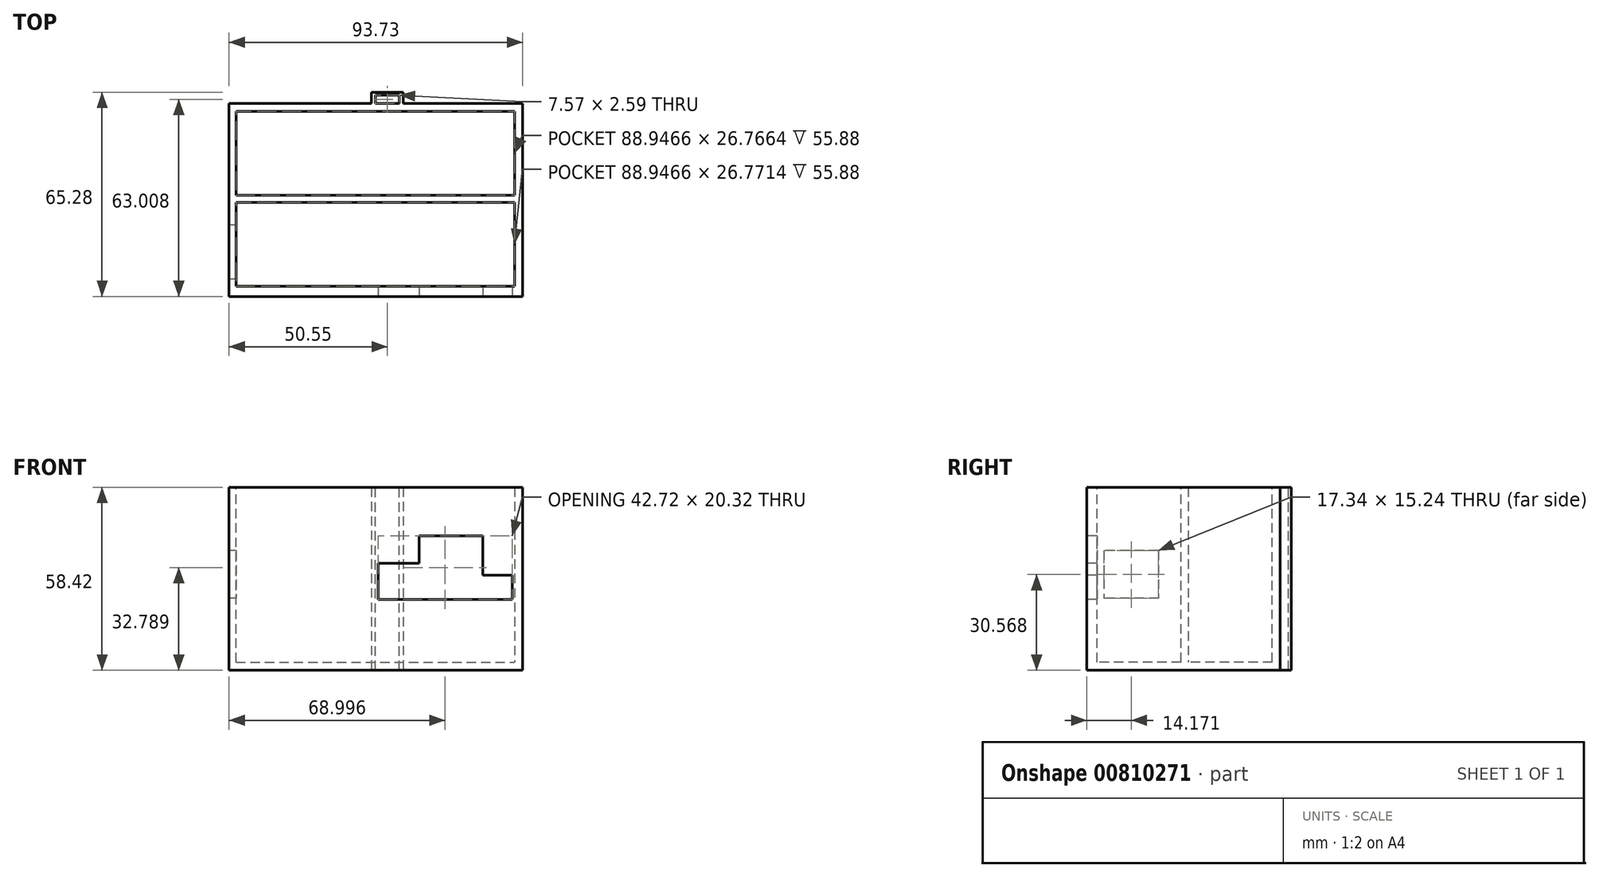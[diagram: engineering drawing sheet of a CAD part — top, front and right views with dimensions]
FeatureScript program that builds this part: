
annotation { "Feature Type Name" : "Feature", "Feature Type Description" : "" }
export const myFeature = defineFeature(function(context is Context, id is Id, definition is map)
    precondition{}
    {
        {
            var Q0;
            Q0=qCreatedBy(makeId("Front.planeOp"),FACE);
            var sketch = newSketch(context, id + "F0", { "sketchPlane" : qUnion([Q0])});
            skLineSegment(sketch, "E0.bottom", {"start": v(-45.72, 29.21) * mm, "end": v(40.64, 29.21) * mm});
            skLineSegment(sketch, "E0.top", {"start": v(-45.72, -29.21) * mm, "end": v(40.64, -29.21) * mm});
            skLineSegment(sketch, "E0.left", {"start": v(-45.72, 29.21) * mm, "end": v(-45.72, -29.21) * mm});
            skLineSegment(sketch, "E0.right", {"start": v(40.64, 29.21) * mm, "end": v(40.64, -29.21) * mm});
            skPoint(sketch, "E0.middle", {"position": v(-2.54, 0) * mm});
            skSolve(sketch);
        }
        {
            var Q0;
            Q0=makeQuery(id+"F0.imprint","IMPRINT",FACE,{"disambiguationData":[TD([[makeQuery(id+"F0.imprint","IMPRINT",EDGE,{"derivedFrom":sQuery(id+"F0.wireOp",EDGE,"E0.bottom")}),-1.0]])]});
            extrude(context, id + "F1", {"entities" : qUnion([Q0]), "oppositeDirection" : true, "depth" : 61.72 * mm, "offsetDistance" : 25.4 * mm});
        }
        {
            var Q0;
            Q0=makeQuery(id+"F1.opExtrude","CAP_FACE",FACE,{"disambiguationData":[OSD([sQuery(id+"F0.wireOp",EDGE,"E0.bottom"),sQuery(id+"F0.wireOp",EDGE,"E0.top"),sQuery(id+"F0.wireOp",EDGE,"E0.left"),sQuery(id+"F0.wireOp",EDGE,"E0.right")])],"isStart":true});
            var sketch = newSketch(context, id + "F2", { "sketchPlane" : qUnion([Q0])});
            skLineSegment(sketch, "E1", {"start": v(-45.72, 29.21) * mm, "end": v(-45.72, 13.74) * mm});
            skLineSegment(sketch, "E2", {"start": v(7.56, 13.74) * mm, "end": v(27.88, 13.74) * mm});
            skLineSegment(sketch, "E3", {"start": v(27.88, 13.74) * mm, "end": v(27.88, -6.58) * mm});
            skLineSegment(sketch, "E4", {"start": v(27.88, -6.58) * mm, "end": v(7.56, -6.58) * mm});
            skLineSegment(sketch, "E5", {"start": v(7.56, -6.58) * mm, "end": v(7.56, 13.74) * mm});
            skLineSegment(sketch, "E6", {"start": v(27.88, 1.12) * mm, "end": v(27.88, -6.58) * mm});
            skLineSegment(sketch, "E7", {"start": v(37.27, 1.12) * mm, "end": v(37.27, -6.58) * mm});
            skLineSegment(sketch, "E8", {"start": v(27.88, 1.12) * mm, "end": v(37.27, 1.12) * mm});
            skLineSegment(sketch, "E9", {"start": v(37.27, -6.58) * mm, "end": v(27.88, -6.58) * mm});
            skLineSegment(sketch, "E10.bottom", {"start": v(7.56, -6.58) * mm, "end": v(-5.45, -6.58) * mm});
            skLineSegment(sketch, "E10.top", {"start": v(7.56, 4.93) * mm, "end": v(-5.45, 4.93) * mm});
            skLineSegment(sketch, "E10.left", {"start": v(7.56, -6.58) * mm, "end": v(7.56, 4.93) * mm});
            skLineSegment(sketch, "E10.right", {"start": v(-5.45, -6.58) * mm, "end": v(-5.45, 4.93) * mm});
            skSolve(sketch);
        }
        {
            var Q0;
            Q0 = qSketchRegion(id + "F2", true);
            extrude(context, id + "F3", {"entities" : qUnion([Q0]), "operationType" : NewBodyOperationType.REMOVE, "oppositeDirection" : true, "depth" : 56.64 * mm, "offsetDistance" : 25.4 * mm});
        }
        {
            var Q0;
            Q0=makeQuery(id+"F1.opExtrude","SWEPT_FACE",FACE,{"disambiguationData":[OSD([sQuery(id+"F0.wireOp",EDGE,"E0.bottom")])]});
            var sketch = newSketch(context, id + "F4", { "sketchPlane" : qUnion([Q0])});
            skLineSegment(sketch, "E11", {"start": v(-43.12, 0) * mm, "end": v(37.96, 0) * mm});
            skLineSegment(sketch, "E12", {"start": v(37.96, 61.72) * mm, "end": v(-43.18, 61.72) * mm});
            skLineSegment(sketch, "E13", {"start": v(-43.18, 59.18) * mm, "end": v(38.1, 59.18) * mm});
            skLineSegment(sketch, "E14", {"start": v(38.1, 3.3) * mm, "end": v(-43.18, 3.3) * mm});
            skLineSegment(sketch, "E15", {"start": v(-43.18, 59.18) * mm, "end": v(-43.18, 3.3) * mm});
            skLineSegment(sketch, "E16", {"start": v(38.1, 59.18) * mm, "end": v(38.1, 3.3) * mm});
            skSolve(sketch);
        }
        {
            var Q0;
            Q0 = qSketchRegion(id + "F4", true);
            extrude(context, id + "F5", {"entities" : qUnion([Q0]), "operationType" : NewBodyOperationType.REMOVE, "oppositeDirection" : true, "depth" : 55.88 * mm, "offsetDistance" : 25.4 * mm});
        }
        {
            var Q0;
            Q0=makeQuery(id+"F5.boolean.opBoolean","COPY",FACE,{"derivedFrom":makeQuery(id+"F5.opExtrude","CAP_FACE",FACE,{"disambiguationData":[OSD([sQuery(id+"F4.wireOp",EDGE,"E13"),sQuery(id+"F4.wireOp",EDGE,"E14"),sQuery(id+"F4.wireOp",EDGE,"E15"),sQuery(id+"F4.wireOp",EDGE,"E16")])],"isStart":false})});
            var sketch = newSketch(context, id + "F6", { "sketchPlane" : qUnion([Q0])});
            skLineSegment(sketch, "E17", {"start": v(-43.18, 16.72) * mm, "end": v(-43.18, 32.42) * mm});
            skLineSegment(sketch, "E18", {"start": v(-43.18, 32.42) * mm, "end": v(38.1, 32.42) * mm});
            skLineSegment(sketch, "E19", {"start": v(38.1, 32.42) * mm, "end": v(38.1, 16.72) * mm});
            skLineSegment(sketch, "E20", {"start": v(-43.18, 30.07) * mm, "end": v(38.1, 30.07) * mm});
            skSolve(sketch);
        }
        {
            var Q0;
            Q0 = qSketchRegion(id + "F6", true);
            extrude(context, id + "F7", {"entities" : qUnion([Q0]), "operationType" : NewBodyOperationType.ADD, "depth" : 55.88 * mm, "offsetDistance" : 25.4 * mm});
        }
        {
            var Q0;
            Q0=makeQuery(id+"F1.opExtrude","CAP_FACE",FACE,{"disambiguationData":[OSD([sQuery(id+"F0.wireOp",EDGE,"E0.bottom"),sQuery(id+"F0.wireOp",EDGE,"E0.top"),sQuery(id+"F0.wireOp",EDGE,"E0.left"),sQuery(id+"F0.wireOp",EDGE,"E0.right")])],"isStart":false});
            var sketch = newSketch(context, id + "F8", { "sketchPlane" : qUnion([Q0])});
            skLineSegment(sketch, "E21", {"start": v(-2.54, 29.21) * mm, "end": v(-2.54, 20.53) * mm});
            skLineSegment(sketch, "E22", {"start": v(-2.54, 20.53) * mm, "end": v(7.62, 20.53) * mm});
            skLineSegment(sketch, "E23", {"start": v(7.62, 20.53) * mm, "end": v(7.62, 29.21) * mm});
            skLineSegment(sketch, "E24.top", {"start": v(-2.54, -29.21) * mm, "end": v(7.62, -29.21) * mm});
            skLineSegment(sketch, "E24.left", {"start": v(-2.54, 20.53) * mm, "end": v(-2.54, -29.21) * mm});
            skLineSegment(sketch, "E24.right", {"start": v(7.62, 20.53) * mm, "end": v(7.62, -29.21) * mm});
            skSolve(sketch);
        }
        {
            var Q0;
            Q0=makeQuery(id+"F8.imprint","IMPRINT",FACE,{"disambiguationData":[TD([[makeQuery(id+"F8.imprint","IMPRINT",EDGE,{"derivedFrom":sQuery(id+"F8.wireOp",EDGE,"E24.top")}),-1.0]])]});
            var Q1;
            {var subQ0=sQuery(id+"F8.wireOp",EDGE,"E21");Q1=makeQuery(id+"F8.imprint","IMPRINT",FACE,{"disambiguationData":[TD([[makeQuery(id+"F8.imprint","IMPRINT",EDGE,{"derivedFrom":subQ0}),1.0]])]});}
            extrude(context, id + "F9", {"entities" : qUnion([Q0, Q1]), "operationType" : NewBodyOperationType.ADD, "depth" : 3.56 * mm, "offsetDistance" : 25.4 * mm});
        }
        {
            var Q0;
            {var subQ0=sQuery(id+"F0.wireOp",EDGE,"E0.bottom");Q0=makeQuery(id+"F9.boolean.opBoolean","MERGE",FACE,{"derivedFrom":[makeQuery(id+"F7.boolean.opBoolean","MERGE",FACE,{"derivedFrom":[makeQuery(id+"F1.opExtrude","SWEPT_FACE",FACE,{"disambiguationData":[OSD([subQ0])]}),makeQuery(id+"F7.opExtrude","CAP_FACE",FACE,{"disambiguationData":[OSD([sQuery(id+"F6.wireOp",EDGE,"E17"),sQuery(id+"F6.wireOp",EDGE,"E18"),sQuery(id+"F6.wireOp",EDGE,"E19"),sQuery(id+"F6.wireOp",EDGE,"E20")])],"isStart":false})]}),makeQuery(id+"F9.opExtrude","SWEPT_FACE",FACE,{"disambiguationData":[OSD([subQ0])]})]});}
            var sketch = newSketch(context, id + "F10", { "sketchPlane" : qUnion([Q0])});
            skLineSegment(sketch, "E25.bottom", {"start": v(-6.32, 64.3) * mm, "end": v(1.24, 64.3) * mm});
            skLineSegment(sketch, "E25.top", {"start": v(-6.32, 62.7) * mm, "end": v(1.24, 62.7) * mm});
            skLineSegment(sketch, "E25.left", {"start": v(-6.32, 64.3) * mm, "end": v(-6.32, 62.7) * mm});
            skLineSegment(sketch, "E25.right", {"start": v(1.24, 64.3) * mm, "end": v(1.24, 62.7) * mm});
            skPoint(sketch, "E25.middle", {"position": v(-2.54, 63.5) * mm});
            skPoint(sketch, "E25.middle.positionSnap0", {"position": v(2.54, 63.5) * mm});
            skPoint(sketch, "E25.middle.positionSnap1", {"position": v(-2.54, 65.28) * mm});
            skPoint(sketch, "E25.centerSnap0", {"position": v(2.54, 63.5) * mm});
            skPoint(sketch, "E25.centerSnap1", {"position": v(-2.54, 65.28) * mm});
            skLineSegment(sketch, "E26", {"start": v(-6.32, 62.7) * mm, "end": v(-6.32, 61.71) * mm});
            skLineSegment(sketch, "E27", {"start": v(-6.32, 61.71) * mm, "end": v(1.24, 61.71) * mm});
            skLineSegment(sketch, "E28", {"start": v(1.24, 61.71) * mm, "end": v(1.24, 62.7) * mm});
            skSolve(sketch);
        }
        {
            var Q0;
            Q0 = qSketchRegion(id + "F10", true);
            extrude(context, id + "F11", {"entities" : qUnion([Q0]), "operationType" : NewBodyOperationType.REMOVE, "oppositeDirection" : true, "depth" : 69.34 * mm, "offsetDistance" : 25.4 * mm});
        }
        {
            var Q0;
            Q0=makeQuery(id+"F1.opExtrude","SWEPT_FACE",FACE,{"disambiguationData":[OSD([sQuery(id+"F0.wireOp",EDGE,"E0.left")])]});
            extrude(context, id + "F12", {"entities" : qUnion([Q0]), "operationType" : NewBodyOperationType.ADD, "depth" : 7.37 * mm, "offsetDistance" : 25.4 * mm});
        }
        {
            var Q0;
            {var subQ0=sQuery(id+"F0.wireOp",EDGE,"E0.bottom");Q0=makeQuery(id+"F12.boolean.opBoolean","MERGE",FACE,{"derivedFrom":[makeQuery(id+"F9.boolean.opBoolean","MERGE",FACE,{"derivedFrom":[makeQuery(id+"F7.boolean.opBoolean","MERGE",FACE,{"derivedFrom":[makeQuery(id+"F1.opExtrude","SWEPT_FACE",FACE,{"disambiguationData":[OSD([subQ0])]}),makeQuery(id+"F7.opExtrude","CAP_FACE",FACE,{"disambiguationData":[OSD([sQuery(id+"F6.wireOp",EDGE,"E17"),sQuery(id+"F6.wireOp",EDGE,"E18"),sQuery(id+"F6.wireOp",EDGE,"E19"),sQuery(id+"F6.wireOp",EDGE,"E20")])],"isStart":false})]}),makeQuery(id+"F9.opExtrude","SWEPT_FACE",FACE,{"disambiguationData":[OSD([subQ0])]})]}),makeQuery(id+"F12.opExtrude","SWEPT_FACE",FACE,{"disambiguationData":[OSD([subQ0,sQuery(id+"F0.wireOp",EDGE,"E0.left")])]})]});}
            var sketch = newSketch(context, id + "F13", { "sketchPlane" : qUnion([Q0])});
            skLineSegment(sketch, "E29.bottom", {"start": v(-50.85, 59.18) * mm, "end": v(-43.18, 59.18) * mm});
            skLineSegment(sketch, "E29.top", {"start": v(-50.85, 3.3) * mm, "end": v(-43.18, 3.3) * mm});
            skLineSegment(sketch, "E29.left", {"start": v(-50.85, 59.18) * mm, "end": v(-50.85, 3.3) * mm});
            skLineSegment(sketch, "E29.right", {"start": v(-43.18, 59.18) * mm, "end": v(-43.18, 3.3) * mm});
            skLineSegment(sketch, "E30", {"start": v(-43.18, 32.42) * mm, "end": v(-50.85, 32.42) * mm});
            skLineSegment(sketch, "E31", {"start": v(-50.85, 32.42) * mm, "end": v(-50.85, 30.07) * mm});
            skLineSegment(sketch, "E32", {"start": v(-50.85, 30.07) * mm, "end": v(-43.18, 30.07) * mm});
            skLineSegment(sketch, "E33", {"start": v(-43.18, 30.07) * mm, "end": v(-43.18, 32.42) * mm});
            skSolve(sketch);
        }
        {
            var Q0;
            {var subQ0=sQuery(id+"F13.wireOp",EDGE,"E29.top");Q0=makeQuery(id+"F13.imprint","IMPRINT",FACE,{"disambiguationData":[TD([[makeQuery(id+"F13.imprint","IMPRINT",EDGE,{"derivedFrom":subQ0}),1.0]])]});}
            extrude(context, id + "F14", {"entities" : qUnion([Q0]), "operationType" : NewBodyOperationType.REMOVE, "oppositeDirection" : true, "depth" : 55.88 * mm, "offsetDistance" : 25.4 * mm});
        }
        {
            var Q0;
            {var subQ0=sQuery(id+"F0.wireOp",EDGE,"E0.bottom");Q0=makeQuery(id+"F12.boolean.opBoolean","MERGE",FACE,{"derivedFrom":[makeQuery(id+"F9.boolean.opBoolean","MERGE",FACE,{"derivedFrom":[makeQuery(id+"F7.boolean.opBoolean","MERGE",FACE,{"derivedFrom":[makeQuery(id+"F1.opExtrude","SWEPT_FACE",FACE,{"disambiguationData":[OSD([subQ0])]}),makeQuery(id+"F7.opExtrude","CAP_FACE",FACE,{"disambiguationData":[OSD([sQuery(id+"F6.wireOp",EDGE,"E17"),sQuery(id+"F6.wireOp",EDGE,"E18"),sQuery(id+"F6.wireOp",EDGE,"E19"),sQuery(id+"F6.wireOp",EDGE,"E20")])],"isStart":false})]}),makeQuery(id+"F9.opExtrude","SWEPT_FACE",FACE,{"disambiguationData":[OSD([subQ0])]})]}),makeQuery(id+"F12.opExtrude","SWEPT_FACE",FACE,{"disambiguationData":[OSD([subQ0,sQuery(id+"F0.wireOp",EDGE,"E0.left")])]})]});}
            var sketch = newSketch(context, id + "F15", { "sketchPlane" : qUnion([Q0])});
            skLineSegment(sketch, "E34.bottom", {"start": v(-50.85, 59.18) * mm, "end": v(-43.18, 59.18) * mm});
            skLineSegment(sketch, "E34.top", {"start": v(-50.85, 32.42) * mm, "end": v(-43.18, 32.42) * mm});
            skLineSegment(sketch, "E34.left", {"start": v(-50.85, 59.18) * mm, "end": v(-50.85, 32.42) * mm});
            skLineSegment(sketch, "E34.right", {"start": v(-43.18, 59.18) * mm, "end": v(-43.18, 32.42) * mm});
            skSolve(sketch);
        }
        {
            var Q0;
            Q0 = qSketchRegion(id + "F15", true);
            extrude(context, id + "F16", {"entities" : qUnion([Q0]), "operationType" : NewBodyOperationType.REMOVE, "oppositeDirection" : true, "depth" : 55.88 * mm, "offsetDistance" : 25.4 * mm});
        }
        {
            var Q0;
            Q0=makeQuery(id+"F12.opExtrude","CAP_FACE",FACE,{"disambiguationData":[OSD([sQuery(id+"F0.wireOp",EDGE,"E0.left")])],"isStart":false});
            var sketch = newSketch(context, id + "F17", { "sketchPlane" : qUnion([Q0])});
            skLineSegment(sketch, "E35.bottom", {"start": v(-22.84, 8.98) * mm, "end": v(-5.5, 8.98) * mm});
            skLineSegment(sketch, "E35.top", {"start": v(-22.84, -6.26) * mm, "end": v(-5.5, -6.26) * mm});
            skLineSegment(sketch, "E35.left", {"start": v(-22.84, 8.98) * mm, "end": v(-22.84, -6.26) * mm});
            skLineSegment(sketch, "E35.right", {"start": v(-5.5, 8.98) * mm, "end": v(-5.5, -6.26) * mm});
            skPoint(sketch, "E35.middle", {"position": v(-14.17, 1.36) * mm});
            skSolve(sketch);
        }
        {
            var Q0;
            Q0 = qSketchRegion(id + "F17", true);
            extrude(context, id + "F18", {"entities" : qUnion([Q0]), "operationType" : NewBodyOperationType.REMOVE, "oppositeDirection" : true, "depth" : 25.4 * mm, "offsetDistance" : 25.4 * mm});
        }
    });
